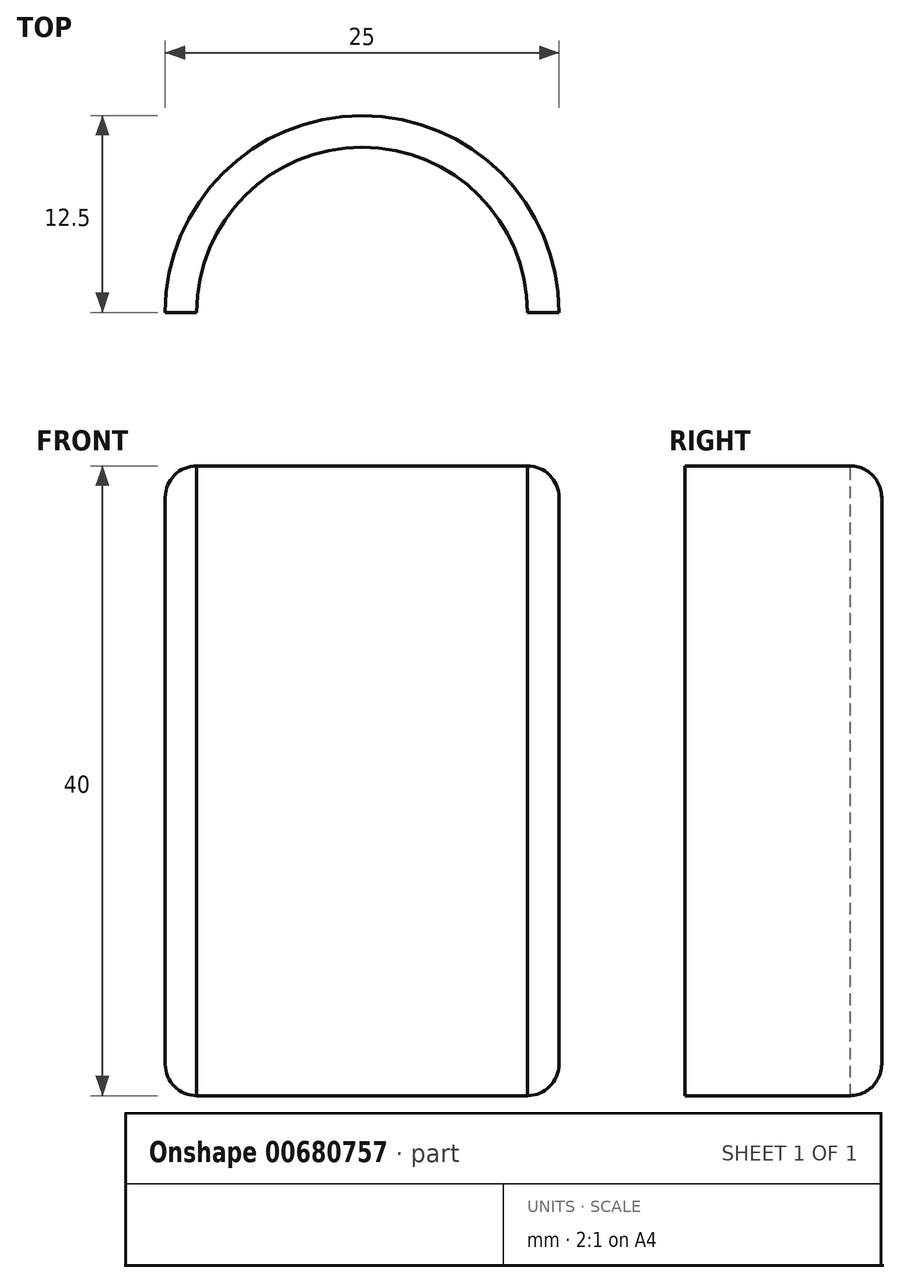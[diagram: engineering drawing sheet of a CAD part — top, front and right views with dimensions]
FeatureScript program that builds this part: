
annotation { "Feature Type Name" : "Feature", "Feature Type Description" : "" }
export const myFeature = defineFeature(function(context is Context, id is Id, definition is map)
    precondition{}
    {
        {
            var Q0;
            Q0=qCreatedBy(makeId("Front.planeOp"),FACE);
            var sketch = newSketch(context, id + "F0", { "sketchPlane" : qUnion([Q0])});
            skLineSegment(sketch, "E0.bottom", {"start": v(-4.25, 20) * mm, "end": v(6.25, 20) * mm});
            skLineSegment(sketch, "E0.top", {"start": v(-4.25, -20) * mm, "end": v(6.25, -20) * mm});
            skLineSegment(sketch, "E0.left", {"start": v(-6.25, 18) * mm, "end": v(-6.25, -18) * mm});
            skLineSegment(sketch, "E0.right", {"start": v(6.25, 20) * mm, "end": v(6.25, -20) * mm});
            skPoint(sketch, "E0.middle", {"position": v(0, 0) * mm});
            skPoint(sketch, "E1.visualSharp", {"position": v(-6.25, 20) * mm});
            skArc(sketch, "E1.filletArc", {"start": v(-4.25, 20) * mm, "mid": v(-5.66, 19.41) * mm, "end": v(-6.25, 18) * mm});
            skPoint(sketch, "E2.visualSharp", {"position": v(-6.25, -20) * mm});
            skArc(sketch, "E2.filletArc", {"start": v(-6.25, -18) * mm, "mid": v(-5.66, -19.41) * mm, "end": v(-4.25, -20) * mm});
            skSolve(sketch);
        }
        {
            var Q0;
            Q0=makeQuery(id+"F0.imprint","IMPRINT",FACE,{"disambiguationData":[TD([[makeQuery(id+"F0.imprint","IMPRINT",EDGE,{"derivedFrom":sQuery(id+"F0.wireOp",EDGE,"E0.bottom")}),-1.0]])]});
            var Q1;
            Q1=sQuery(id+"F0.wireOp",EDGE,"E0.right");
            revolve(context, id + "F1", {"entities" : qUnion([Q0]), "axis" : qUnion([Q1]), "revolveType" : RevolveType.ONE_DIRECTION, "angle" : 180 * degree});
        }
        {
            var Q0;
            Q0=makeQuery(id+"F1.opRevolve","SWEPT_FACE",FACE,{"disambiguationData":[OSD([sQuery(id+"F0.wireOp",EDGE,"E0.bottom")])]});
            var sketch = newSketch(context, id + "F2", { "sketchPlane" : qUnion([Q0])});
            skCircle(sketch, "E3", {"center": v(6.25, 0) * mm, "radius": 10.5 * mm});
            skLineSegment(sketch, "E4", {"start": v(-4.25, 0) * mm, "end": v(16.75, 0) * mm});
            skSolve(sketch);
        }
        {
            var Q0;
            Q0 = qSketchRegion(id + "F2", true);
            extrude(context, id + "F3", {"entities" : qUnion([Q0]), "operationType" : NewBodyOperationType.REMOVE, "oppositeDirection" : true, "depth" : 40 * mm, "offsetDistance" : 25 * mm});
        }
    });
